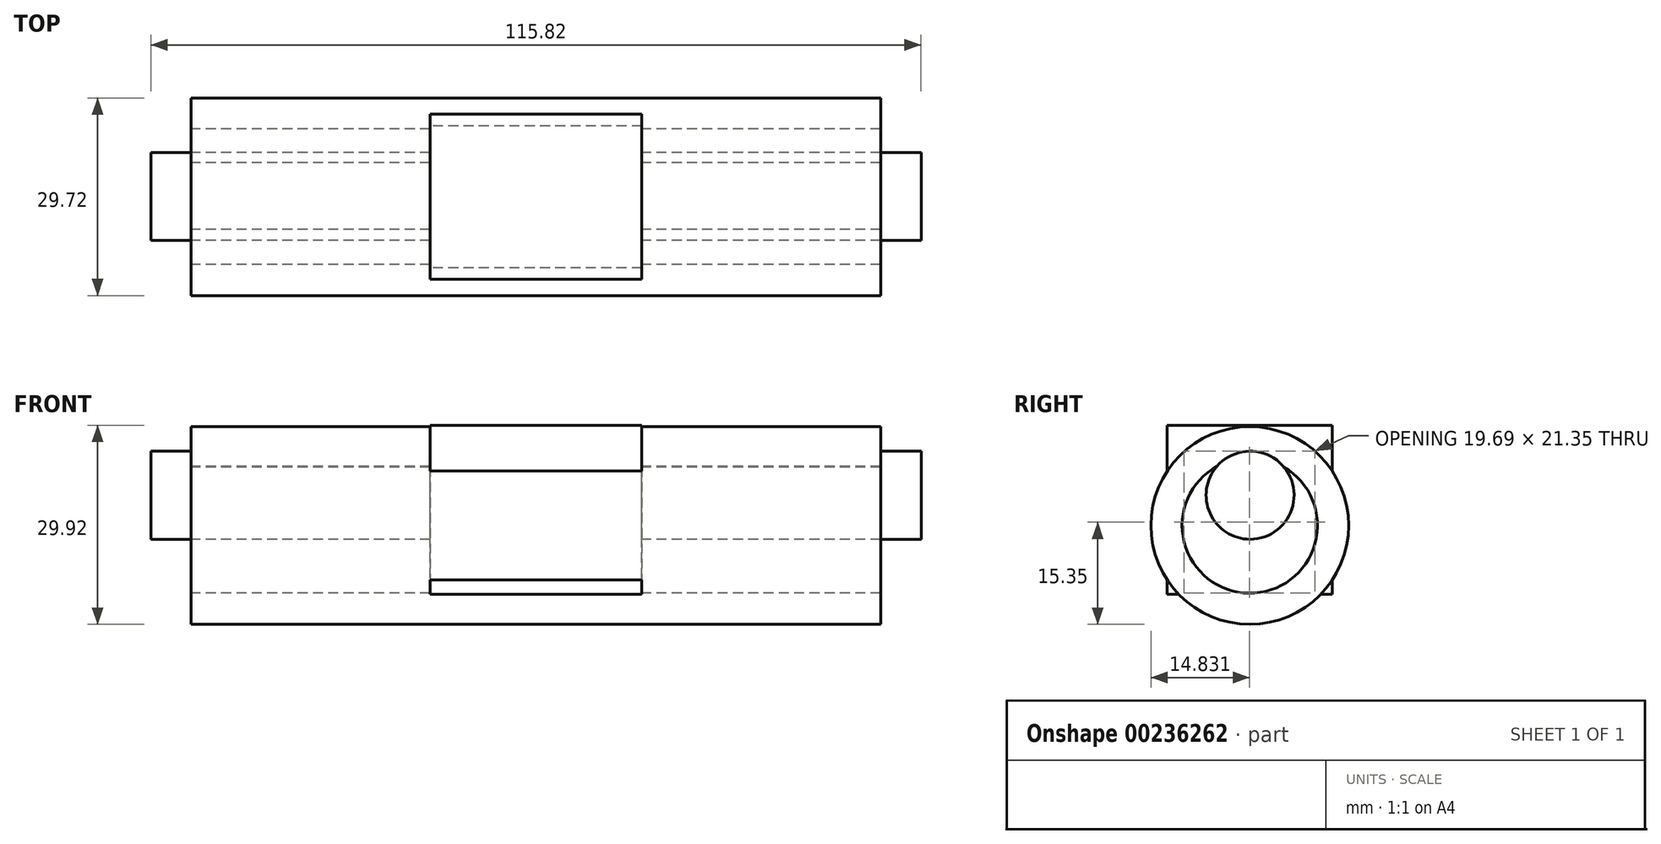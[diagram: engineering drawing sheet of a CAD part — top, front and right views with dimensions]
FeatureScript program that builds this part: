
annotation { "Feature Type Name" : "Feature", "Feature Type Description" : "" }
export const myFeature = defineFeature(function(context is Context, id is Id, definition is map)
    precondition{}
    {
        {
            var Q0;
            Q0=qCreatedBy(makeId("Top.planeOp"),FACE);
            var sketch = newSketch(context, id + "F0", { "sketchPlane" : qUnion([Q0])});
            skLineSegment(sketch, "E0.bottom", {"start": v(15.92, -12.4) * mm, "end": v(-15.92, -12.4) * mm});
            skLineSegment(sketch, "E0.top", {"start": v(15.92, 12.4) * mm, "end": v(-15.92, 12.4) * mm});
            skLineSegment(sketch, "E0.left", {"start": v(15.92, -12.4) * mm, "end": v(15.92, 12.4) * mm});
            skLineSegment(sketch, "E0.right", {"start": v(-15.92, -12.4) * mm, "end": v(-15.92, 12.4) * mm});
            skPoint(sketch, "E0.middle", {"position": v(0, 0) * mm});
            skSolve(sketch);
        }
        {
            var Q0;
            Q0 = qSketchRegion(id + "F0", true);
            extrude(context, id + "F1", {"entities" : qUnion([Q0]), "depth" : 25.4 * mm});
        }
        {
            var Q0;
            Q0=qCreatedBy(makeId("Right.planeOp"),FACE);
            var sketch = newSketch(context, id + "F2", { "sketchPlane" : qUnion([Q0])});
            skCircle(sketch, "E1", {"center": v(0.05, 14.89) * mm, "radius": 6.62 * mm});
            skPoint(sketch, "E1.first.point", {"position": v(-6, 12.2) * mm});
            skPoint(sketch, "E1.second.point", {"position": v(6.62, 15.71) * mm});
            skPoint(sketch, "E1.third.point", {"position": v(0, 8.27) * mm});
            skSolve(sketch);
        }
        {
            var Q0;
            Q0 = qSketchRegion(id + "F2", true);
            extrude(context, id + "F3", {"entities" : qUnion([Q0]), "operationType" : NewBodyOperationType.ADD, "endBound" : BoundingType.SYMMETRIC, "depth" : 81.28 * mm});
        }
        {
            var Q0;
            Q0=makeQuery(id+"F3.opExtrude","CAP_FACE",FACE,{"disambiguationData":[OSD([sQuery(id+"F2.wireOp",EDGE,"E1")])],"isStart":true});
            var Q1;
            Q1=makeQuery(id+"F3.opExtrude","CAP_FACE",FACE,{"disambiguationData":[OSD([sQuery(id+"F2.wireOp",EDGE,"E1")])],"isStart":false});
            extrude(context, id + "F4", {"entities" : qUnion([Q0, Q1]), "operationType" : NewBodyOperationType.ADD, "endBound" : BoundingType.SYMMETRIC, "oppositeDirection" : true, "depth" : 34.54 * mm});
        }
        {
            var Q0;
            Q0=qCreatedBy(makeId("Right.planeOp"),FACE);
            var sketch = newSketch(context, id + "F5", { "sketchPlane" : qUnion([Q0])});
            skCircle(sketch, "E2", {"center": v(0, 10.34) * mm, "radius": 14.86 * mm});
            skCircle(sketch, "E3", {"center": v(0, 10.34) * mm, "radius": 10.18 * mm});
            skSolve(sketch);
        }
        {
            var Q0;
            Q0 = qSketchRegion(id + "F5", true);
            extrude(context, id + "F6", {"entities" : qUnion([Q0]), "operationType" : NewBodyOperationType.ADD, "endBound" : BoundingType.SYMMETRIC, "depth" : 103.63 * mm});
        }
    });
